# Revit family: 3-1202-xx Perla Mirror
name_source: partatom
category: Luminarias
units: mm (PartAtom-declared; Revit-internal decimal feet)

## family parameters
Anfitrión = Muro
Compartido = No
Corte con vacíos al cargar = No
Cota de conector redondo = Diámetro de uso
Número OmniClass = 23.80.70.00
Origen de luz = No
Punto de cálculo de habitación = No
Siempre vertical = Sí
Tipo de pieza = Normal
Título OmniClass = Lighting

## types (1)
- 3-1202-0 / Black
    Comentarios de vataje = 1 x 35.3 W at 120 V
    Diameter = 914 mm  [stored 2.99869 ft]
    Elevación por defecto = 0 mm  [stored 0 ft]
    Fabricante = Vanita by Oxygen
    Lámpara = LED Array
    Metal Finish 1 = 15 - Black
    Modelo = 3-120X-xx / Perla
    References = Ref. 3 = 120 V / Ref. 37 = 277 V
    URL = www.oxygenlighting.com
    Voltage = 120 V
    Voltage Input = 120 V or 277 V - 50/60 Hz

note: [stored X ft] marks values corroborated as IEEE doubles in the binary element streams (Revit-internal decimal feet)

## geometry (parser evidence)
native form markers: Sweep x4
no freeform markers — native parametric forms only
